# Revit family: SystemSchroeders_Wandklappe
name_source: partatom
category: HLS-Bauteile
revit_build: Autodesk Revit 2018 (Build: 20170223_1515(x64)
units: mm (PartAtom-declared; Revit-internal decimal feet)

## family parameters
Basisbauteil = Wand
Beim Laden mit Abzugskörper schneiden = Nein
Bemaßung runder Anschluss = Durchmesser verwenden
Gemeinsam genutzt = Nein
Immer vertikal = Nein
Klassifizierung = Keine
Raumberechnungspunkt = Nein
Teiletyp = Normal

## types (12) — shared parameters
Abdeckung = 26 mm
Breite Rahmen = 730 mm
Breite Öffnung = 760 mm
Einbauhöhe = 1600 mm  [stored 5.24934 ft]
Gopen = 15 mm  [stored 0.0492126 ft]
Hersteller = System Schröders
Höhe Öffnung = 760 mm
URL = https://www.system-schroeders.de
Werkstoff Griff/Schloss = Edelstahl
Werkstoff Klappenblatt = Edelstahl
Werkstoff Rahmen = Edelstahl
a1 = 24 mm

## per-type parameters (varying)
| type | Dicke Blatt | Druck- / Sogwiderstand | Einbruchschutz | Feuerschutz | Luftdichtigkeit | Rauchschutz | Schallschutz | Schlagregendichtheit | Widerstandsfähigkeit gegen Winlast |
| TSN-1 CE | 65 mm  [stored 0.213255 ft] | 5000Pa | RC4 RC3 RC2 RC1 | EI2 60 -S a -C5 | bis Klasse 4 (600 Pa) | S200 | 53 (-1;-5) dB | bis Klasse 8A | bis Klasse C5 (2.000 Pa) |
| ESN-1 | 65 mm  [stored 0.213255 ft] | 5000Pa | RC4 RC3 RC2 RC1 | - | bis Klasse 4 (600 Pa) | - | 53 (-1;-5) dB | bis Klasse 8A | bis Klasse C5 (2.000 Pa) |
| EIS-11 | 65 mm  [stored 0.213255 ft] | 5000Pa | - | EI2 120 -S a -C5 | bis Klasse 4 (600 Pa) | S200 | - | bis Klasse 8A | bis Klasse C5 (2.000 Pa) |
| ASN-1 | 65 mm  [stored 0.213255 ft] | 5000Pa | - | - | bis Klasse 4 (600 Pa) | - | - | bis Klasse 8A | bis Klasse C5 (2.000 Pa) |
| TSN-3 CE | 65 mm  [stored 0.213255 ft] | 5000Pa | RC4 RC3 RC2 RC1 | EI2 60 -S a -C5 | bis Klasse 4 (600 Pa) | S200 | 53 (-1;-5) dB | bis Klasse 8A | bis Klasse C5 (2.000 Pa) |
| TSN-1 | 65 mm  [stored 0.213255 ft] | 5000Pa | RC4 RC3 RC2 RC1 | T-30 | bis Klasse 4 (600 Pa) | RS | 53 (-1;-5) dB |  |  |
| TSN-11 | 65 mm  [stored 0.213255 ft] | 5000Pa | RC4 RC3 RC2 RC1 | T-90 | bis Klasse 4 (600 Pa) | RS | 53 (-1;-5) dB |  |  |
| TSN-11 CE | 65 mm  [stored 0.213255 ft] | 5000Pa | RC4 RC3 RC2 RC1 | EI2 90 -S a -C5 | bis Klasse 4 (600 Pa) | S200 | 53 (-1;-5) dB | bis Klasse 8A | bis Klasse C5 (2.000 Pa) |
| SN-1 | 65 mm  [stored 0.213255 ft] | 5000Pa | - | - | bis Klasse 4 (600 Pa) | - | 53 (-1;-5) dB | bis Klasse 8A | bis Klasse C5 (2.000 Pa) |
| RSN-1 | 65 mm  [stored 0.213255 ft] | 5000Pa | RC4 RC3 RC2 RC1 | - | bis Klasse 4 (600 Pa) | RS | 53 (-1;-5) dB | bis Klasse 8A | bis Klasse C5 (2.000 Pa) |
| ISN-1 | 80 mm | - | - | - | bis Klasse 4 (600 Pa) | - | - | bis Klasse 8A | bis Klasse C5 (2.000 Pa) |
| RSN-1 CE | 65 mm  [stored 0.213255 ft] | - | - | - | - | - | - | bis Klasse 8A | bis Klasse C5 (2.000 Pa) |

note: [stored X ft] marks values corroborated as IEEE doubles in the binary element streams (Revit-internal decimal feet)

## geometry (parser evidence)
native form markers: Sweep x3
no freeform markers — native parametric forms only
